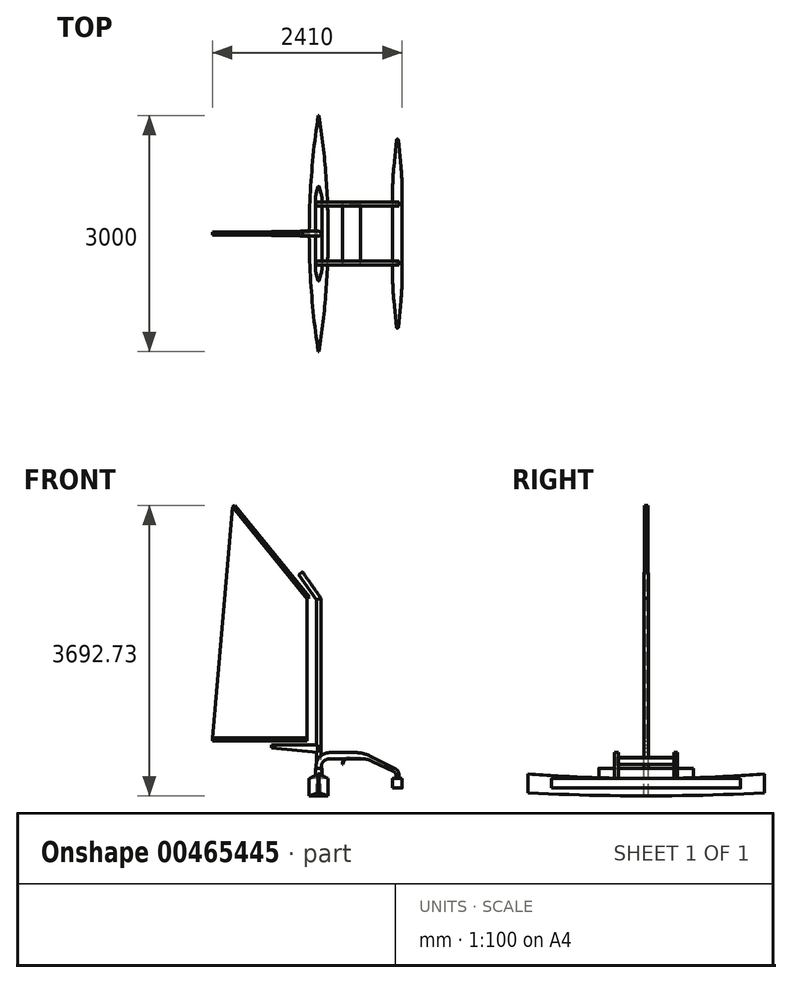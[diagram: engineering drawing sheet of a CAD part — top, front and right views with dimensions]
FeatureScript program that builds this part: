
annotation { "Feature Type Name" : "Feature", "Feature Type Description" : "" }
export const myFeature = defineFeature(function(context is Context, id is Id, definition is map)
    precondition{}
    {
        {
            var Q0;
            Q0=qCreatedBy(makeId("Top.planeOp"),FACE);
            var sketch = newSketch(context, id + "F0", { "sketchPlane" : qUnion([Q0])});
            skLineSegment(sketch, "E0", {"start": v(0, 0) * mm, "end": v(0, 1500) * mm});
            skLineSegment(sketch, "E1", {"start": v(0, 0) * mm, "end": v(120, 0) * mm});
            skLineSegment(sketch, "E2", {"start": v(120, 0) * mm, "end": v(120, -200) * mm, "construction": true});
            skLineSegment(sketch, "E3", {"start": v(0, 1500) * mm, "end": v(5, 1500) * mm});
            skArc(sketch, "E4", {"start": v(120, 0) * mm, "mid": v(91.2, 752.2) * mm, "end": v(5, 1500) * mm});
            skSolve(sketch);
        }
        {
            var Q0;
            Q0=qSketchRegion(id+"F0",true);
            extrude(context, id + "F1", {"entities" : qUnion([Q0]), "depth" : 110 * mm});
        }
        {
            var Q0;
            Q0=qCreatedBy(makeId("Right.planeOp"),FACE);
            var sketch = newSketch(context, id + "F2", { "sketchPlane" : qUnion([Q0])});
            skLineSegment(sketch, "E5.0", {"start": v(0, 0) * mm, "end": v(1500, 0) * mm});
            skLineSegment(sketch, "E6", {"start": v(1500, 0) * mm, "end": v(1500, 40) * mm});
            skLineSegment(sketch, "E7", {"start": v(0, 0) * mm, "end": v(-216.61, 0) * mm, "construction": true});
            skArc(sketch, "E8", {"start": v(0, 0) * mm, "mid": v(750.27, 10) * mm, "end": v(1500, 40) * mm});
            skSolve(sketch);
        }
        {
            var Q0;
            Q0=qSketchRegion(id+"F2",true);
            extrude(context, id + "F3", {"entities" : qUnion([Q0]), "operationType" : NewBodyOperationType.REMOVE, "depth" : 200 * mm});
        }
        {
            var Q0;
            Q0=makeQuery(id+"F1.opExtrude","SWEPT_BODY",BODY,{"disambiguationData":[OSD([sQuery(id+"F0.wireOp",EDGE,"E0"),sQuery(id+"F0.wireOp",EDGE,"E1"),sQuery(id+"F0.wireOp",EDGE,"E3"),sQuery(id+"F0.wireOp",EDGE,"E4")])]});
            var Q1;
            Q1=makeQuery(id+"F1.opExtrude","CAP_FACE",FACE,{"disambiguationData":[OSD([sQuery(id+"F0.wireOp",EDGE,"E0"),sQuery(id+"F0.wireOp",EDGE,"E1"),sQuery(id+"F0.wireOp",EDGE,"E3"),sQuery(id+"F0.wireOp",EDGE,"E4")])],"isStart":false});
            mirror(context, id + "F4", {"operationType" : NewBodyOperationType.ADD, "entities" : qUnion([Q0]), "mirrorPlane" : qUnion([Q1])});
        }
        {
            var Q0;
            Q0=makeQuery(id+"F1.opExtrude","SWEPT_BODY",BODY,{"disambiguationData":[OSD([sQuery(id+"F0.wireOp",EDGE,"E0"),sQuery(id+"F0.wireOp",EDGE,"E1"),sQuery(id+"F0.wireOp",EDGE,"E3"),sQuery(id+"F0.wireOp",EDGE,"E4")])]});
            var Q1;
            Q1=qCreatedBy(makeId("Right.planeOp"),FACE);
            mirror(context, id + "F5", {"operationType" : NewBodyOperationType.ADD, "entities" : qUnion([Q0]), "mirrorPlane" : qUnion([Q1])});
        }
        {
            var Q0;
            Q0=makeQuery(id+"F1.opExtrude","SWEPT_BODY",BODY,{"disambiguationData":[OSD([sQuery(id+"F0.wireOp",EDGE,"E0"),sQuery(id+"F0.wireOp",EDGE,"E1"),sQuery(id+"F0.wireOp",EDGE,"E3"),sQuery(id+"F0.wireOp",EDGE,"E4")])]});
            var Q1;
            Q1=qCreatedBy(makeId("Front.planeOp"),FACE);
            mirror(context, id + "F6", {"operationType" : NewBodyOperationType.ADD, "entities" : qUnion([Q0]), "mirrorPlane" : qUnion([Q1])});
        }
        {
            var Q0;
            Q0=qCreatedBy(makeId("Right.planeOp"),FACE);
            var sketch = newSketch(context, id + "F7", { "sketchPlane" : qUnion([Q0])});
            skLineSegment(sketch, "E9", {"start": v(-1500, 180) * mm, "end": v(-1500, 280) * mm});
            skLineSegment(sketch, "E10", {"start": v(1500, 180) * mm, "end": v(1500, 280) * mm});
            skLineSegment(sketch, "E11", {"start": v(0, 0) * mm, "end": v(0, 220) * mm, "construction": true});
            skArc(sketch, "E12", {"start": v(-1500, 280) * mm, "mid": v(0, 220) * mm, "end": v(1500, 280) * mm});
            skLineSegment(sketch, "E13", {"start": v(-1500, 180) * mm, "end": v(1500, 180) * mm});
            skSolve(sketch);
        }
        {
            var Q0;
            Q0 = qSketchRegion(id + "F7", true);
            extrude(context, id + "F8", {"entities" : qUnion([Q0]), "operationType" : NewBodyOperationType.ADD, "depth" : 200 * mm, "hasSecondDirection" : true, "secondDirectionOppositeDirection" : true, "secondDirectionDepth" : 200 * mm});
        }
        {
            var Q0;
            Q0=makeQuery(id+"F8.opExtrude","SWEPT_FACE",FACE,{"disambiguationData":[OSD([sQuery(id+"F7.wireOp",EDGE,"E13")])]});
            var sketch = newSketch(context, id + "F9", { "sketchPlane" : qUnion([Q0])});
            skLineSegment(sketch, "E14.0", {"start": v(200, 1500) * mm, "end": v(200, -1500) * mm});
            skLineSegment(sketch, "E15.0", {"start": v(5, -1500) * mm, "end": v(-5, -1500) * mm});
            skLineSegment(sketch, "E16.0", {"start": v(-200, 1500) * mm, "end": v(-200, -1500) * mm});
            skArc(sketch, "E17.0", {"start": v(5, -1500) * mm, "mid": v(120, 0) * mm, "end": v(5, 1500) * mm});
            skArc(sketch, "E18.0", {"start": v(-5, 1500) * mm, "mid": v(-120, 0) * mm, "end": v(-5, -1500) * mm});
            skLineSegment(sketch, "E19.0", {"start": v(5, 1500) * mm, "end": v(-5, 1500) * mm});
            skLineSegment(sketch, "E20", {"start": v(-200, 1500) * mm, "end": v(-200, 1658.3) * mm});
            skLineSegment(sketch, "E21", {"start": v(-200, 1658.3) * mm, "end": v(200, 1658.3) * mm});
            skLineSegment(sketch, "E22", {"start": v(200, 1500) * mm, "end": v(200, 1658.3) * mm});
            skPoint(sketch, "E23.orphan", {"position": v(211.73, 1658.3) * mm});
            skLineSegment(sketch, "E24", {"start": v(-200, -1500) * mm, "end": v(-200, -1609.33) * mm});
            skLineSegment(sketch, "E25", {"start": v(200, -1500) * mm, "end": v(200, -1609.33) * mm});
            skLineSegment(sketch, "E26", {"start": v(-200, -1609.33) * mm, "end": v(200, -1609.33) * mm});
            skSolve(sketch);
        }
        {
            var Q0;
            Q0 = qSketchRegion(id + "F9", true);
            extrude(context, id + "F10", {"entities" : qUnion([Q0]), "operationType" : NewBodyOperationType.REMOVE, "oppositeDirection" : true, "depth" : 200 * mm});
        }
        {
            var Q0;
            Q0=qCreatedBy(makeId("Top.planeOp"),FACE);
            cPlane(context, id + "F11", {"entities" : qUnion([Q0]), "cplaneType" : CPlaneType.OFFSET, "offset" : 100 * mm, "width" : 150 * mm, "height" : 150 * mm});
        }
        {
            var Q0;
            Q0=qCreatedBy(id+"F11.planeOp",FACE);
            var sketch = newSketch(context, id + "F12", { "sketchPlane" : qUnion([Q0])});
            skLineSegment(sketch, "E27.bottom", {"start": v(40, -600) * mm, "end": v(-40, -600) * mm});
            skLineSegment(sketch, "E27.top", {"start": v(40, 600) * mm, "end": v(-40, 600) * mm});
            skLineSegment(sketch, "E27.left", {"start": v(40, -600) * mm, "end": v(40, 600) * mm});
            skLineSegment(sketch, "E27.right", {"start": v(-40, -600) * mm, "end": v(-40, 600) * mm});
            skPoint(sketch, "E27.middle", {"position": v(0, 0) * mm});
            skSolve(sketch);
        }
        {
            var Q0;
            Q0 = qSketchRegion(id + "F12", true);
            extrude(context, id + "F13", {"entities" : qUnion([Q0]), "operationType" : NewBodyOperationType.ADD, "depth" : 250 * mm});
        }
        {
            var Q0;
            Q0=makeQuery(id+"F13.opExtrude","SWEPT_EDGE",EDGE,{"disambiguationData":[OSD([sQuery(id+"F12.wireOp",EDGE,"E27.bottom"),sQuery(id+"F12.wireOp",EDGE,"E27.left")])]});
            var Q1;
            Q1=makeQuery(id+"F13.opExtrude","SWEPT_EDGE",EDGE,{"disambiguationData":[OSD([sQuery(id+"F12.wireOp",EDGE,"E27.bottom"),sQuery(id+"F12.wireOp",EDGE,"E27.right")])]});
            var Q2;
            Q2=makeQuery(id+"F13.opExtrude","SWEPT_EDGE",EDGE,{"disambiguationData":[OSD([sQuery(id+"F12.wireOp",EDGE,"E27.top"),sQuery(id+"F12.wireOp",EDGE,"E27.right")])]});
            var Q3;
            Q3=makeQuery(id+"F13.opExtrude","SWEPT_EDGE",EDGE,{"disambiguationData":[OSD([sQuery(id+"F12.wireOp",EDGE,"E27.top"),sQuery(id+"F12.wireOp",EDGE,"E27.left")])]});
            chamfer(context, id + "F14", {"entities" : qUnion([Q0, Q1, Q2, Q3]), "chamferType" : ChamferType.TWO_OFFSETS, "width1" : 35 * mm, "oppositeDirection" : true, "width2" : 120 * mm, "tangentPropagation" : true});
        }
        {
            var Q0;
            {var subQ0=sQuery(id+"F12.wireOp",EDGE,"E27.top");Q0=makeQuery(id+"F14.opChamfer","BLEND_EDGE",EDGE,{"blendedFrom":[makeQuery(id+"F13.opExtrude","SWEPT_EDGE",EDGE,{"disambiguationData":[OSD([subQ0,sQuery(id+"F12.wireOp",EDGE,"E27.right")])]}),makeQuery(id+"F13.opExtrude","SWEPT_FACE",FACE,{"disambiguationData":[OSD([subQ0])]})],"blendedInto":[makeQuery(id+"F13.opExtrude","SWEPT_FACE",FACE,{"disambiguationData":[OSD([subQ0])]})]});}
            var Q1;
            {var subQ0=sQuery(id+"F12.wireOp",EDGE,"E27.top");Q1=makeQuery(id+"F14.opChamfer","BLEND_EDGE",EDGE,{"blendedFrom":[makeQuery(id+"F13.opExtrude","SWEPT_EDGE",EDGE,{"disambiguationData":[OSD([subQ0,sQuery(id+"F12.wireOp",EDGE,"E27.left")])]}),makeQuery(id+"F13.opExtrude","SWEPT_FACE",FACE,{"disambiguationData":[OSD([subQ0])]})],"blendedInto":[makeQuery(id+"F13.opExtrude","SWEPT_FACE",FACE,{"disambiguationData":[OSD([subQ0])]})]});}
            var Q2;
            {var subQ0=sQuery(id+"F12.wireOp",EDGE,"E27.bottom");Q2=makeQuery(id+"F14.opChamfer","BLEND_EDGE",EDGE,{"blendedFrom":[makeQuery(id+"F13.opExtrude","SWEPT_EDGE",EDGE,{"disambiguationData":[OSD([subQ0,sQuery(id+"F12.wireOp",EDGE,"E27.right")])]}),makeQuery(id+"F13.opExtrude","SWEPT_FACE",FACE,{"disambiguationData":[OSD([subQ0])]})],"blendedInto":[makeQuery(id+"F13.opExtrude","SWEPT_FACE",FACE,{"disambiguationData":[OSD([subQ0])]})]});}
            var Q3;
            {var subQ0=sQuery(id+"F12.wireOp",EDGE,"E27.bottom");Q3=makeQuery(id+"F14.opChamfer","BLEND_EDGE",EDGE,{"blendedFrom":[makeQuery(id+"F13.opExtrude","SWEPT_EDGE",EDGE,{"disambiguationData":[OSD([subQ0,sQuery(id+"F12.wireOp",EDGE,"E27.left")])]}),makeQuery(id+"F13.opExtrude","SWEPT_FACE",FACE,{"disambiguationData":[OSD([subQ0])]})],"blendedInto":[makeQuery(id+"F13.opExtrude","SWEPT_FACE",FACE,{"disambiguationData":[OSD([subQ0])]})]});}
            fillet(context, id + "F15", {"entities" : qUnion([Q0, Q1, Q2, Q3]), "radius" : 5 * mm, "tangentPropagation" : true, "allowEdgeOverflow" : false});
        }
        {
            var Q0;
            {var subQ0=sQuery(id+"F12.wireOp",EDGE,"E27.right");Q0=makeQuery(id+"F14.opChamfer","BLEND_EDGE",EDGE,{"blendedFrom":[makeQuery(id+"F13.opExtrude","SWEPT_EDGE",EDGE,{"disambiguationData":[OSD([sQuery(id+"F12.wireOp",EDGE,"E27.bottom"),subQ0])]}),makeQuery(id+"F13.opExtrude","SWEPT_FACE",FACE,{"disambiguationData":[OSD([subQ0])]})],"blendedInto":[makeQuery(id+"F13.opExtrude","SWEPT_FACE",FACE,{"disambiguationData":[OSD([subQ0])]})]});}
            var Q1;
            {var subQ0=sQuery(id+"F12.wireOp",EDGE,"E27.left");Q1=makeQuery(id+"F14.opChamfer","BLEND_EDGE",EDGE,{"blendedFrom":[makeQuery(id+"F13.opExtrude","SWEPT_EDGE",EDGE,{"disambiguationData":[OSD([sQuery(id+"F12.wireOp",EDGE,"E27.bottom"),subQ0])]}),makeQuery(id+"F13.opExtrude","SWEPT_FACE",FACE,{"disambiguationData":[OSD([subQ0])]})],"blendedInto":[makeQuery(id+"F13.opExtrude","SWEPT_FACE",FACE,{"disambiguationData":[OSD([subQ0])]})]});}
            var Q2;
            {var subQ0=sQuery(id+"F12.wireOp",EDGE,"E27.left");Q2=makeQuery(id+"F14.opChamfer","BLEND_EDGE",EDGE,{"blendedFrom":[makeQuery(id+"F13.opExtrude","SWEPT_EDGE",EDGE,{"disambiguationData":[OSD([sQuery(id+"F12.wireOp",EDGE,"E27.top"),subQ0])]}),makeQuery(id+"F13.opExtrude","SWEPT_FACE",FACE,{"disambiguationData":[OSD([subQ0])]})],"blendedInto":[makeQuery(id+"F13.opExtrude","SWEPT_FACE",FACE,{"disambiguationData":[OSD([subQ0])]})]});}
            var Q3;
            {var subQ0=sQuery(id+"F12.wireOp",EDGE,"E27.right");Q3=makeQuery(id+"F14.opChamfer","BLEND_EDGE",EDGE,{"blendedFrom":[makeQuery(id+"F13.opExtrude","SWEPT_EDGE",EDGE,{"disambiguationData":[OSD([sQuery(id+"F12.wireOp",EDGE,"E27.top"),subQ0])]}),makeQuery(id+"F13.opExtrude","SWEPT_FACE",FACE,{"disambiguationData":[OSD([subQ0])]})],"blendedInto":[makeQuery(id+"F13.opExtrude","SWEPT_FACE",FACE,{"disambiguationData":[OSD([subQ0])]})]});}
            fillet(context, id + "F16", {"entities" : qUnion([Q0, Q1, Q2, Q3]), "radius" : 200 * mm, "tangentPropagation" : true, "allowEdgeOverflow" : false});
        }
        {
            var Q0;
            Q0=qCreatedBy(id+"F11.planeOp",FACE);
            var sketch = newSketch(context, id + "F17", { "sketchPlane" : qUnion([Q0])});
            skLineSegment(sketch, "E28.bottom", {"start": v(1060, 1200) * mm, "end": v(940, 1200) * mm});
            skLineSegment(sketch, "E28.top", {"start": v(1060, -1200) * mm, "end": v(940, -1200) * mm});
            skLineSegment(sketch, "E28.left", {"start": v(1060, 1200) * mm, "end": v(1060, -1200) * mm});
            skLineSegment(sketch, "E28.right", {"start": v(940, 1200) * mm, "end": v(940, -1200) * mm});
            skPoint(sketch, "E28.middle", {"position": v(1000, 0) * mm});
            skSolve(sketch);
        }
        {
            var Q0;
            Q0 = qSketchRegion(id + "F17", true);
            extrude(context, id + "F18", {"entities" : qUnion([Q0]), "depth" : 120 * mm});
        }
        {
            var Q0;
            Q0=makeQuery(id+"F18.opExtrude","SWEPT_EDGE",EDGE,{"disambiguationData":[OSD([sQuery(id+"F17.wireOp",EDGE,"E28.top"),sQuery(id+"F17.wireOp",EDGE,"E28.right")])]});
            var Q1;
            Q1=makeQuery(id+"F18.opExtrude","SWEPT_EDGE",EDGE,{"disambiguationData":[OSD([sQuery(id+"F17.wireOp",EDGE,"E28.top"),sQuery(id+"F17.wireOp",EDGE,"E28.left")])]});
            var Q2;
            Q2=makeQuery(id+"F18.opExtrude","SWEPT_EDGE",EDGE,{"disambiguationData":[OSD([sQuery(id+"F17.wireOp",EDGE,"E28.bottom"),sQuery(id+"F17.wireOp",EDGE,"E28.right")])]});
            var Q3;
            Q3=makeQuery(id+"F18.opExtrude","SWEPT_EDGE",EDGE,{"disambiguationData":[OSD([sQuery(id+"F17.wireOp",EDGE,"E28.bottom"),sQuery(id+"F17.wireOp",EDGE,"E28.left")])]});
            chamfer(context, id + "F19", {"entities" : qUnion([Q0, Q1, Q2, Q3]), "chamferType" : ChamferType.TWO_OFFSETS, "width1" : 50 * mm, "oppositeDirection" : false, "width2" : 500 * mm, "tangentPropagation" : true});
        }
        {
            var Q0;
            {var subQ0=sQuery(id+"F17.wireOp",EDGE,"E28.top");Q0=makeQuery(id+"F19.opChamfer","BLEND_EDGE",EDGE,{"blendedFrom":[makeQuery(id+"F18.opExtrude","SWEPT_EDGE",EDGE,{"disambiguationData":[OSD([subQ0,sQuery(id+"F17.wireOp",EDGE,"E28.right")])]}),makeQuery(id+"F18.opExtrude","SWEPT_FACE",FACE,{"disambiguationData":[OSD([subQ0])]})],"blendedInto":[makeQuery(id+"F18.opExtrude","SWEPT_FACE",FACE,{"disambiguationData":[OSD([subQ0])]})]});}
            var Q1;
            {var subQ0=sQuery(id+"F17.wireOp",EDGE,"E28.top");Q1=makeQuery(id+"F19.opChamfer","BLEND_EDGE",EDGE,{"blendedFrom":[makeQuery(id+"F18.opExtrude","SWEPT_EDGE",EDGE,{"disambiguationData":[OSD([subQ0,sQuery(id+"F17.wireOp",EDGE,"E28.left")])]}),makeQuery(id+"F18.opExtrude","SWEPT_FACE",FACE,{"disambiguationData":[OSD([subQ0])]})],"blendedInto":[makeQuery(id+"F18.opExtrude","SWEPT_FACE",FACE,{"disambiguationData":[OSD([subQ0])]})]});}
            var Q2;
            {var subQ0=sQuery(id+"F17.wireOp",EDGE,"E28.bottom");Q2=makeQuery(id+"F19.opChamfer","BLEND_EDGE",EDGE,{"blendedFrom":[makeQuery(id+"F18.opExtrude","SWEPT_EDGE",EDGE,{"disambiguationData":[OSD([subQ0,sQuery(id+"F17.wireOp",EDGE,"E28.right")])]}),makeQuery(id+"F18.opExtrude","SWEPT_FACE",FACE,{"disambiguationData":[OSD([subQ0])]})],"blendedInto":[makeQuery(id+"F18.opExtrude","SWEPT_FACE",FACE,{"disambiguationData":[OSD([subQ0])]})]});}
            var Q3;
            {var subQ0=sQuery(id+"F17.wireOp",EDGE,"E28.bottom");Q3=makeQuery(id+"F19.opChamfer","BLEND_EDGE",EDGE,{"blendedFrom":[makeQuery(id+"F18.opExtrude","SWEPT_EDGE",EDGE,{"disambiguationData":[OSD([subQ0,sQuery(id+"F17.wireOp",EDGE,"E28.left")])]}),makeQuery(id+"F18.opExtrude","SWEPT_FACE",FACE,{"disambiguationData":[OSD([subQ0])]})],"blendedInto":[makeQuery(id+"F18.opExtrude","SWEPT_FACE",FACE,{"disambiguationData":[OSD([subQ0])]})]});}
            fillet(context, id + "F20", {"entities" : qUnion([Q0, Q1, Q2, Q3]), "radius" : 10 * mm, "tangentPropagation" : true, "allowEdgeOverflow" : false});
        }
        {
            var Q0;
            {var subQ0=sQuery(id+"F17.wireOp",EDGE,"E28.left");Q0=makeQuery(id+"F19.opChamfer","BLEND_EDGE",EDGE,{"blendedFrom":[makeQuery(id+"F18.opExtrude","SWEPT_EDGE",EDGE,{"disambiguationData":[OSD([sQuery(id+"F17.wireOp",EDGE,"E28.bottom"),subQ0])]}),makeQuery(id+"F18.opExtrude","SWEPT_FACE",FACE,{"disambiguationData":[OSD([subQ0])]})],"blendedInto":[makeQuery(id+"F18.opExtrude","SWEPT_FACE",FACE,{"disambiguationData":[OSD([subQ0])]})]});}
            var Q1;
            {var subQ0=sQuery(id+"F17.wireOp",EDGE,"E28.right");Q1=makeQuery(id+"F19.opChamfer","BLEND_EDGE",EDGE,{"blendedFrom":[makeQuery(id+"F18.opExtrude","SWEPT_EDGE",EDGE,{"disambiguationData":[OSD([sQuery(id+"F17.wireOp",EDGE,"E28.bottom"),subQ0])]}),makeQuery(id+"F18.opExtrude","SWEPT_FACE",FACE,{"disambiguationData":[OSD([subQ0])]})],"blendedInto":[makeQuery(id+"F18.opExtrude","SWEPT_FACE",FACE,{"disambiguationData":[OSD([subQ0])]})]});}
            var Q2;
            {var subQ0=sQuery(id+"F17.wireOp",EDGE,"E28.right");Q2=makeQuery(id+"F19.opChamfer","BLEND_EDGE",EDGE,{"blendedFrom":[makeQuery(id+"F18.opExtrude","SWEPT_EDGE",EDGE,{"disambiguationData":[OSD([sQuery(id+"F17.wireOp",EDGE,"E28.top"),subQ0])]}),makeQuery(id+"F18.opExtrude","SWEPT_FACE",FACE,{"disambiguationData":[OSD([subQ0])]})],"blendedInto":[makeQuery(id+"F18.opExtrude","SWEPT_FACE",FACE,{"disambiguationData":[OSD([subQ0])]})]});}
            var Q3;
            {var subQ0=sQuery(id+"F17.wireOp",EDGE,"E28.left");Q3=makeQuery(id+"F19.opChamfer","BLEND_EDGE",EDGE,{"blendedFrom":[makeQuery(id+"F18.opExtrude","SWEPT_EDGE",EDGE,{"disambiguationData":[OSD([sQuery(id+"F17.wireOp",EDGE,"E28.top"),subQ0])]}),makeQuery(id+"F18.opExtrude","SWEPT_FACE",FACE,{"disambiguationData":[OSD([subQ0])]})],"blendedInto":[makeQuery(id+"F18.opExtrude","SWEPT_FACE",FACE,{"disambiguationData":[OSD([subQ0])]})]});}
            fillet(context, id + "F21", {"entities" : qUnion([Q0, Q1, Q2, Q3]), "radius" : 3000 * mm, "tangentPropagation" : true, "allowEdgeOverflow" : false});
        }
        {
            var Q0;
            Q0=qCreatedBy(makeId("Front.planeOp"),FACE);
            cPlane(context, id + "F22", {"entities" : qUnion([Q0]), "cplaneType" : CPlaneType.OFFSET, "offset" : 400 * mm, "width" : 150 * mm, "height" : 150 * mm});
        }
        {
            var Q0;
            Q0=qCreatedBy(id+"F22.planeOp",FACE);
            var sketch = newSketch(context, id + "F23", { "sketchPlane" : qUnion([Q0])});
            skLineSegment(sketch, "E29", {"start": v(33.27, 350) * mm, "end": v(-33.27, 350) * mm});
            skLineSegment(sketch, "E30", {"start": v(1020, 220) * mm, "end": v(980, 220) * mm});
            skLineSegment(sketch, "E31", {"start": v(-33.27, 350) * mm, "end": v(-33.27, 380) * mm});
            skLineSegment(sketch, "E32", {"start": v(136.73, 550) * mm, "end": v(475.83, 550) * mm});
            skLineSegment(sketch, "E33", {"start": v(33.27, 350) * mm, "end": v(33.27, 370) * mm});
            skLineSegment(sketch, "E34", {"start": v(980, 220) * mm, "end": v(980, 268.3) * mm});
            skLineSegment(sketch, "E35", {"start": v(1020, 220) * mm, "end": v(1020, 270.88) * mm});
            skPoint(sketch, "E36.orphan", {"position": v(1060, 220) * mm});
            skPoint(sketch, "E37.orphan", {"position": v(940, 220) * mm});
            skLineSegment(sketch, "E38", {"start": v(647.78, 508.87) * mm, "end": v(976.2, 342.23) * mm});
            skLineSegment(sketch, "E39", {"start": v(133.27, 470) * mm, "end": v(552.25, 470) * mm});
            skLineSegment(sketch, "E40", {"start": v(680.18, 441.35) * mm, "end": v(951.32, 313.52) * mm});
            skPoint(sketch, "E41.visualSharp", {"position": v(33.27, 470) * mm});
            skArc(sketch, "E41.filletArc", {"start": v(133.27, 470) * mm, "mid": v(62.56, 440.71) * mm, "end": v(33.27, 370) * mm});
            skPoint(sketch, "E42.visualSharp", {"position": v(-33.27, 550) * mm});
            skArc(sketch, "E42.filletArc", {"start": v(136.73, 550) * mm, "mid": v(16.52, 500.2) * mm, "end": v(-33.27, 380) * mm});
            skPoint(sketch, "E43.visualSharp", {"position": v(619.42, 470) * mm});
            skArc(sketch, "E43.filletArc", {"start": v(680.18, 441.35) * mm, "mid": v(617.8, 462.75) * mm, "end": v(552.25, 470) * mm});
            skPoint(sketch, "E44.visualSharp", {"position": v(566.73, 550) * mm});
            skArc(sketch, "E44.filletArc", {"start": v(647.78, 508.87) * mm, "mid": v(564.23, 539.57) * mm, "end": v(475.83, 550) * mm});
            skPoint(sketch, "E45.visualSharp", {"position": v(980, 300) * mm});
            skArc(sketch, "E45.filletArc", {"start": v(980, 268.3) * mm, "mid": v(972.23, 295.07) * mm, "end": v(951.32, 313.52) * mm});
            skPoint(sketch, "E46.visualSharp", {"position": v(1020, 320) * mm});
            skArc(sketch, "E46.filletArc", {"start": v(1020, 270.88) * mm, "mid": v(1008.18, 312.74) * mm, "end": v(976.2, 342.23) * mm});
            skSolve(sketch);
        }
        {
            var Q0;
            Q0 = qSketchRegion(id + "F23", true);
            extrude(context, id + "F24", {"entities" : qUnion([Q0]), "oppositeDirection" : true, "depth" : 50 * mm});
        }
        {
            var Q0;
            Q0=makeQuery(id+"F24.opExtrude","SWEPT_BODY",BODY,{"disambiguationData":[OSD([sQuery(id+"F23.wireOp",EDGE,"E29"),sQuery(id+"F23.wireOp",EDGE,"E30"),sQuery(id+"F23.wireOp",EDGE,"E31"),sQuery(id+"F23.wireOp",EDGE,"E32"),sQuery(id+"F23.wireOp",EDGE,"E33"),sQuery(id+"F23.wireOp",EDGE,"E34"),sQuery(id+"F23.wireOp",EDGE,"E35"),sQuery(id+"F23.wireOp",EDGE,"E38"),sQuery(id+"F23.wireOp",EDGE,"E39"),sQuery(id+"F23.wireOp",EDGE,"E40"),sQuery(id+"F23.wireOp",EDGE,"E41.filletArc"),sQuery(id+"F23.wireOp",EDGE,"E42.filletArc"),sQuery(id+"F23.wireOp",EDGE,"E43.filletArc"),sQuery(id+"F23.wireOp",EDGE,"E44.filletArc"),sQuery(id+"F23.wireOp",EDGE,"E45.filletArc"),sQuery(id+"F23.wireOp",EDGE,"E46.filletArc")])]});
            var Q1;
            Q1=qCreatedBy(makeId("Front.planeOp"),FACE);
            mirror(context, id + "F25", {"entities" : qUnion([Q0]), "mirrorPlane" : qUnion([Q1])});
        }
        {
            var Q0;
            Q0=qCreatedBy(makeId("Front.planeOp"),FACE);
            var sketch = newSketch(context, id + "F26", { "sketchPlane" : qUnion([Q0])});
            skLineSegment(sketch, "E47", {"start": v(0, 0) * mm, "end": v(0, 2500) * mm});
            skLineSegment(sketch, "E48", {"start": v(0, 2500) * mm, "end": v(-229.43, 2827.66) * mm});
            skPoint(sketch, "E49.visualSharp", {"position": v(0, 2500) * mm});
            skSolve(sketch);
        }
        {
            var Q0;
            Q0=makeQuery(id+"F13.opExtrude","CAP_FACE",FACE,{"disambiguationData":[OSD([sQuery(id+"F12.wireOp",EDGE,"E27.bottom"),sQuery(id+"F12.wireOp",EDGE,"E27.top"),sQuery(id+"F12.wireOp",EDGE,"E27.left"),sQuery(id+"F12.wireOp",EDGE,"E27.right")])],"isStart":false});
            var sketch = newSketch(context, id + "F27", { "sketchPlane" : qUnion([Q0])});
            skCircle(sketch, "E50", {"center": v(0, 0) * mm, "radius": 30 * mm});
            skSolve(sketch);
        }
        {
            var Q0;
            Q0 = qSketchRegion(id + "F27", true);
            var Q1;
            Q1 = qBodyType(qCreatedBy(id + "F26" ,EDGE), BodyType.WIRE);
            sweep(context, id + "F28", {"profiles" : qUnion([Q0]), "path" : qUnion([Q1])});
        }
        {
            var Q0;
            Q0=qCreatedBy(makeId("Front.planeOp"),FACE);
            var sketch = newSketch(context, id + "F29", { "sketchPlane" : qUnion([Q0])});
            skLineSegment(sketch, "E51", {"start": v(-118.86, 2525.11) * mm, "end": v(-1060.5, 3692.73) * mm});
            skLineSegment(sketch, "E52", {"start": v(-1060.5, 3692.73) * mm, "end": v(-1091.63, 3667.62) * mm});
            skLineSegment(sketch, "E53", {"start": v(-1091.63, 3667.62) * mm, "end": v(-150, 2500) * mm});
            skLineSegment(sketch, "E54", {"start": v(-150, 2500) * mm, "end": v(-118.86, 2525.11) * mm});
            skPoint(sketch, "E55.orphan", {"position": v(508.89, 1746.7) * mm});
            skSolve(sketch);
        }
        {
            var Q0;
            Q0 = qSketchRegion(id + "F29", true);
            extrude(context, id + "F30", {"entities" : qUnion([Q0]), "depth" : 20 * mm, "hasSecondDirection" : true, "secondDirectionOppositeDirection" : true, "secondDirectionDepth" : 20 * mm});
        }
        {
            var Q0;
            Q0=qCreatedBy(makeId("Front.planeOp"),FACE);
            var sketch = newSketch(context, id + "F31", { "sketchPlane" : qUnion([Q0])});
            skLineSegment(sketch, "E56", {"start": v(0, 650) * mm, "end": v(-600, 650) * mm});
            skLineSegment(sketch, "E57", {"start": v(-600, 650) * mm, "end": v(-600, 610) * mm});
            skLineSegment(sketch, "E58", {"start": v(-600, 610) * mm, "end": v(0, 550) * mm});
            skLineSegment(sketch, "E59", {"start": v(0, 650) * mm, "end": v(0, 550) * mm});
            skSolve(sketch);
        }
        {
            var Q0;
            Q0 = qSketchRegion(id + "F31", true);
            extrude(context, id + "F32", {"entities" : qUnion([Q0]), "operationType" : NewBodyOperationType.ADD, "depth" : 25 * mm, "hasSecondDirection" : true, "secondDirectionOppositeDirection" : true, "secondDirectionDepth" : 25 * mm});
        }
        {
            var Q0;
            Q0=qCreatedBy(makeId("Front.planeOp"),FACE);
            var sketch = newSketch(context, id + "F33", { "sketchPlane" : qUnion([Q0])});
            skLineSegment(sketch, "E60.bottom", {"start": v(-150, 740) * mm, "end": v(-1350, 740) * mm});
            skLineSegment(sketch, "E60.top", {"start": v(-150, 700) * mm, "end": v(-1350, 700) * mm});
            skLineSegment(sketch, "E60.left", {"start": v(-150, 740) * mm, "end": v(-150, 700) * mm});
            skLineSegment(sketch, "E60.right", {"start": v(-1350, 740) * mm, "end": v(-1350, 700) * mm});
            skSolve(sketch);
        }
        {
            var Q0;
            Q0 = qSketchRegion(id + "F33", true);
            extrude(context, id + "F34", {"entities" : qUnion([Q0]), "depth" : 20 * mm, "hasSecondDirection" : true, "secondDirectionOppositeDirection" : true, "secondDirectionDepth" : 20 * mm});
        }
        {
            var Q0;
            Q0=qCreatedBy(makeId("Front.planeOp"),FACE);
            var sketch = newSketch(context, id + "F35", { "sketchPlane" : qUnion([Q0])});
            skLineSegment(sketch, "E61.0", {"start": v(-1091.63, 3667.62) * mm, "end": v(-150, 2500) * mm});
            skLineSegment(sketch, "E62.0", {"start": v(-150, 740) * mm, "end": v(-1350, 740) * mm});
            skLineSegment(sketch, "E63", {"start": v(-150, 2500) * mm, "end": v(-150, 740) * mm});
            skLineSegment(sketch, "E64", {"start": v(-1091.63, 3667.62) * mm, "end": v(-1350, 740) * mm});
            skSolve(sketch);
        }
        {
            var Q0;
            Q0 = qSketchRegion(id + "F35", true);
            extrude(context, id + "F36", {"entities" : qUnion([Q0]), "depth" : .2 * mm, "hasSecondDirection" : true, "secondDirectionOppositeDirection" : true, "secondDirectionDepth" : .2 * mm});
        }
        {
            var Q0;
            Q0=qCreatedBy(makeId("Front.planeOp"),FACE);
            var sketch = newSketch(context, id + "F37", { "sketchPlane" : qUnion([Q0])});
            skLineSegment(sketch, "E65.bottom", {"start": v(310, 480) * mm, "end": v(528.88, 480) * mm});
            skLineSegment(sketch, "E65.top", {"start": v(300, 490) * mm, "end": v(528.88, 490) * mm});
            skLineSegment(sketch, "E65.left", {"start": v(300, 480) * mm, "end": v(300, 490) * mm});
            skLineSegment(sketch, "E65.right", {"start": v(528.88, 480) * mm, "end": v(528.88, 490) * mm});
            skLineSegment(sketch, "E66", {"start": v(300, 480) * mm, "end": v(300, 397.55) * mm});
            skLineSegment(sketch, "E67", {"start": v(300, 397.55) * mm, "end": v(310, 397.55) * mm});
            skLineSegment(sketch, "E68", {"start": v(310, 397.55) * mm, "end": v(310, 480) * mm});
            skSolve(sketch);
        }
        {
            var Q0;
            Q0 = qSketchRegion(id + "F37", true);
            extrude(context, id + "F38", {"entities" : qUnion([Q0]), "depth" : 390 * mm, "hasSecondDirection" : true, "secondDirectionOppositeDirection" : true, "secondDirectionDepth" : 390 * mm});
        }
        {
            var Q0;
            Q0=makeQuery(id+"F38.opExtrude","SWEPT_EDGE",EDGE,{"disambiguationData":[OSD([sQuery(id+"F37.wireOp",EDGE,"E65.bottom"),sQuery(id+"F37.wireOp",EDGE,"E68")])]});
            fillet(context, id + "F39", {"entities" : qUnion([Q0]), "radius" : 80 * mm, "tangentPropagation" : true, "allowEdgeOverflow" : false});
        }
        {
            var Q0;
            Q0=makeQuery(id+"F38.opExtrude","SWEPT_EDGE",EDGE,{"disambiguationData":[OSD([sQuery(id+"F37.wireOp",EDGE,"E65.top"),sQuery(id+"F37.wireOp",EDGE,"E65.left")])]});
            fillet(context, id + "F40", {"entities" : qUnion([Q0]), "radius" : 90 * mm, "tangentPropagation" : true, "allowEdgeOverflow" : false});
        }
    });
